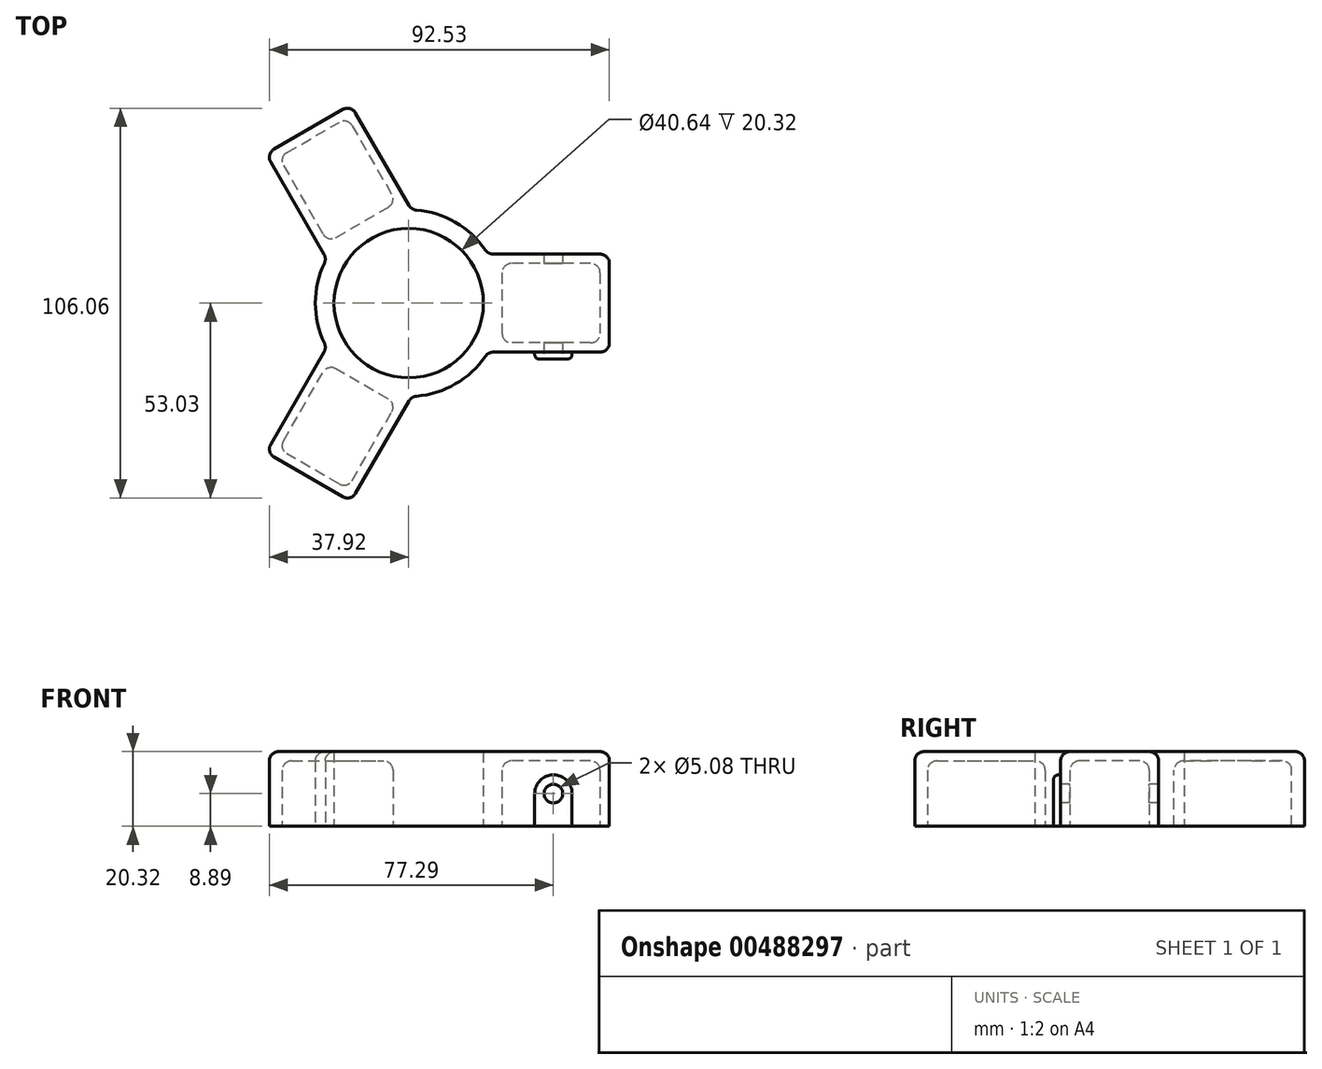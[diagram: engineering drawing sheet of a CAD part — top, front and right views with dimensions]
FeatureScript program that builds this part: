
annotation { "Feature Type Name" : "Feature", "Feature Type Description" : "" }
export const myFeature = defineFeature(function(context is Context, id is Id, definition is map)
    precondition{}
    {
        {
            var Q0;
            Q0=qCreatedBy(makeId("Top.planeOp"),FACE);
            var sketch = newSketch(context, id + "F0", { "sketchPlane" : qUnion([Q0])});
            skCircle(sketch, "E0", {"center": v(0, 0) * mm, "radius": 20.32 * mm});
            skCircle(sketch, "E1.0", {"center": v(0, 0) * mm, "radius": 25.4 * mm});
            skSolve(sketch);
        }
        {
            var Q0;
            Q0=makeQuery(id+"F0.imprint","IMPRINT",FACE,{"disambiguationData":[TD([[makeQuery(id+"F0.imprint","IMPRINT",EDGE,{"derivedFrom":sQuery(id+"F0.wireOp",EDGE,"E0")}),-1.0]])]});
            extrude(context, id + "F1", {"entities" : qUnion([Q0]), "depth" : 20.32 * mm});
        }
        {
            var Q0;
            Q0=qCreatedBy(makeId("Top.planeOp"),FACE);
            var sketch = newSketch(context, id + "F2", { "sketchPlane" : qUnion([Q0])});
            skLineSegment(sketch, "E2.bottom", {"start": v(54.61, 13.34) * mm, "end": v(20.32, 13.34) * mm});
            skLineSegment(sketch, "E2.top", {"start": v(54.61, -13.33) * mm, "end": v(20.32, -13.33) * mm});
            skLineSegment(sketch, "E2.left", {"start": v(54.61, 13.34) * mm, "end": v(54.61, -13.33) * mm});
            skLineSegment(sketch, "E2.right", {"start": v(20.32, 13.34) * mm, "end": v(20.32, -13.33) * mm});
            skPoint(sketch, "E2.middle", {"position": v(37.47, 0) * mm});
            skLineSegment(sketch, "E3.1.0", {"start": v(-21.7, 10.93) * mm, "end": v(1.39, 24.27) * mm});
            skLineSegment(sketch, "E3.1.1", {"start": v(-38.85, 40.63) * mm, "end": v(-15.76, 53.96) * mm});
            skLineSegment(sketch, "E3.1.2", {"start": v(-15.76, 53.96) * mm, "end": v(1.39, 24.27) * mm});
            skLineSegment(sketch, "E3.1.3", {"start": v(-38.85, 40.63) * mm, "end": v(-21.7, 10.93) * mm});
            skPoint(sketch, "E3.1.4", {"position": v(-18.73, 32.45) * mm});
            skLineSegment(sketch, "E3.2.0", {"start": v(1.39, -24.27) * mm, "end": v(-21.7, -10.93) * mm});
            skLineSegment(sketch, "E3.2.1", {"start": v(-15.76, -53.96) * mm, "end": v(-38.85, -40.63) * mm});
            skLineSegment(sketch, "E3.2.2", {"start": v(-38.85, -40.63) * mm, "end": v(-21.7, -10.93) * mm});
            skLineSegment(sketch, "E3.2.3", {"start": v(-15.76, -53.96) * mm, "end": v(1.39, -24.27) * mm});
            skPoint(sketch, "E3.2.4", {"position": v(-18.73, -32.45) * mm});
            skPoint(sketch, "E3.center", {"position": v(0, 0) * mm});
            skLineSegment(sketch, "E4.0", {"start": v(52.07, 10.8) * mm, "end": v(25.4, 10.8) * mm});
            skLineSegment(sketch, "E4.1", {"start": v(52.07, 10.8) * mm, "end": v(52.07, -10.8) * mm});
            skLineSegment(sketch, "E4.2", {"start": v(52.07, -10.8) * mm, "end": v(25.4, -10.8) * mm});
            skLineSegment(sketch, "E4.3", {"start": v(25.4, 10.8) * mm, "end": v(25.4, -10.8) * mm});
            skLineSegment(sketch, "E5.1.0", {"start": v(-35.38, 39.7) * mm, "end": v(-22.05, 16.6) * mm});
            skLineSegment(sketch, "E5.1.2", {"start": v(-35.38, 39.7) * mm, "end": v(-16.69, 50.5) * mm});
            skLineSegment(sketch, "E5.1.3", {"start": v(-16.69, 50.5) * mm, "end": v(-3.35, 27.4) * mm});
            skLineSegment(sketch, "E5.1.4", {"start": v(-22.05, 16.6) * mm, "end": v(-3.35, 27.4) * mm});
            skLineSegment(sketch, "E5.2.0", {"start": v(-16.69, -50.5) * mm, "end": v(-3.35, -27.4) * mm});
            skLineSegment(sketch, "E5.2.2", {"start": v(-16.69, -50.5) * mm, "end": v(-35.38, -39.7) * mm});
            skLineSegment(sketch, "E5.2.3", {"start": v(-35.38, -39.7) * mm, "end": v(-22.05, -16.6) * mm});
            skLineSegment(sketch, "E5.2.4", {"start": v(-3.35, -27.4) * mm, "end": v(-22.05, -16.6) * mm});
            skSolve(sketch);
        }
        {
            var Q0;
            Q0=makeQuery(id+"F2.imprint","IMPRINT",FACE,{"disambiguationData":[TD([[makeQuery(id+"F2.imprint","IMPRINT",EDGE,{"derivedFrom":sQuery(id+"F2.wireOp",EDGE,"E3.1.0")}),1.0]])]});
            var Q1;
            Q1=makeQuery(id+"F2.imprint","IMPRINT",FACE,{"disambiguationData":[TD([[makeQuery(id+"F2.imprint","IMPRINT",EDGE,{"derivedFrom":sQuery(id+"F2.wireOp",EDGE,"E3.2.0")}),1.0]])]});
            var Q2;
            Q2=makeQuery(id+"F2.imprint","IMPRINT",FACE,{"disambiguationData":[TD([[makeQuery(id+"F2.imprint","IMPRINT",EDGE,{"derivedFrom":sQuery(id+"F2.wireOp",EDGE,"E2.bottom")}),1.0]])]});
            extrude(context, id + "F3", {"entities" : qUnion([Q0, Q1, Q2]), "operationType" : NewBodyOperationType.ADD, "depth" : 20.32 * mm});
        }
        {
            var Q0;
            Q0=makeQuery(id+"F3.boolean.opBoolean","MERGE",FACE,{"derivedFrom":[makeQuery(id+"F1.opExtrude","CAP_FACE",FACE,{"disambiguationData":[OSD([sQuery(id+"F0.wireOp",EDGE,"E0"),sQuery(id+"F0.wireOp",EDGE,"E1.0")])],"isStart":false}),makeQuery(id+"F3.opExtrude","CAP_FACE",FACE,{"disambiguationData":[OSD([sQuery(id+"F2.wireOp",EDGE,"E2.bottom"),sQuery(id+"F2.wireOp",EDGE,"E2.top"),sQuery(id+"F2.wireOp",EDGE,"E2.left"),sQuery(id+"F2.wireOp",EDGE,"E2.right"),sQuery(id+"F2.wireOp",EDGE,"E4.0"),sQuery(id+"F2.wireOp",EDGE,"E4.1"),sQuery(id+"F2.wireOp",EDGE,"E4.2"),sQuery(id+"F2.wireOp",EDGE,"E4.3")])],"isStart":false}),makeQuery(id+"F3.opExtrude","CAP_FACE",FACE,{"disambiguationData":[OSD([sQuery(id+"F2.wireOp",EDGE,"E3.1.0"),sQuery(id+"F2.wireOp",EDGE,"E3.1.1"),sQuery(id+"F2.wireOp",EDGE,"E3.1.2"),sQuery(id+"F2.wireOp",EDGE,"E3.1.3"),sQuery(id+"F2.wireOp",EDGE,"E5.1.0"),sQuery(id+"F2.wireOp",EDGE,"E5.1.2"),sQuery(id+"F2.wireOp",EDGE,"E5.1.3"),sQuery(id+"F2.wireOp",EDGE,"E5.1.4")])],"isStart":false}),makeQuery(id+"F3.opExtrude","CAP_FACE",FACE,{"disambiguationData":[OSD([sQuery(id+"F2.wireOp",EDGE,"E3.2.0"),sQuery(id+"F2.wireOp",EDGE,"E3.2.1"),sQuery(id+"F2.wireOp",EDGE,"E3.2.2"),sQuery(id+"F2.wireOp",EDGE,"E3.2.3"),sQuery(id+"F2.wireOp",EDGE,"E5.2.0"),sQuery(id+"F2.wireOp",EDGE,"E5.2.2"),sQuery(id+"F2.wireOp",EDGE,"E5.2.3"),sQuery(id+"F2.wireOp",EDGE,"E5.2.4")])],"isStart":false})]});
            var sketch = newSketch(context, id + "F4", { "sketchPlane" : qUnion([Q0])});
            skLineSegment(sketch, "E6.0", {"start": v(52.07, 10.8) * mm, "end": v(52.07, -10.8) * mm});
            skLineSegment(sketch, "E6.1", {"start": v(52.07, -10.8) * mm, "end": v(25.4, -10.8) * mm});
            skArc(sketch, "E6.2", {"start": v(21.59, -10.78) * mm, "mid": v(24.13, 0) * mm, "end": v(21.6, 10.78) * mm});
            skLineSegment(sketch, "E6.3", {"start": v(52.07, 10.8) * mm, "end": v(25.4, 10.8) * mm});
            skLineSegment(sketch, "E7.1.0", {"start": v(-35.38, 39.7) * mm, "end": v(-16.69, 50.5) * mm});
            skLineSegment(sketch, "E7.1.1", {"start": v(-16.69, 50.5) * mm, "end": v(-3.35, 27.4) * mm});
            skArc(sketch, "E7.1.2", {"start": v(-1.46, 24.09) * mm, "mid": v(-12.06, 20.9) * mm, "end": v(-20.13, 13.3) * mm});
            skLineSegment(sketch, "E7.1.3", {"start": v(-35.38, 39.7) * mm, "end": v(-22.05, 16.6) * mm});
            skLineSegment(sketch, "E7.2.0", {"start": v(-16.69, -50.5) * mm, "end": v(-35.38, -39.7) * mm});
            skLineSegment(sketch, "E7.2.1", {"start": v(-35.38, -39.7) * mm, "end": v(-22.05, -16.6) * mm});
            skArc(sketch, "E7.2.2", {"start": v(-20.13, -13.3) * mm, "mid": v(-12.07, -20.9) * mm, "end": v(-1.46, -24.09) * mm});
            skLineSegment(sketch, "E7.2.3", {"start": v(-16.69, -50.5) * mm, "end": v(-3.35, -27.4) * mm});
            skSolve(sketch);
        }
        {
            var Q0;
            Q0=makeQuery(id+"F4.imprint","IMPRINT",FACE,{"disambiguationData":[TD([[makeQuery(id+"F4.imprint","IMPRINT",EDGE,{"derivedFrom":sQuery(id+"F4.wireOp",EDGE,"E7.1.0")}),-1.0]])]});
            var Q1;
            Q1=makeQuery(id+"F4.imprint","IMPRINT",FACE,{"disambiguationData":[TD([[makeQuery(id+"F4.imprint","IMPRINT",EDGE,{"derivedFrom":sQuery(id+"F4.wireOp",EDGE,"E6.0")}),-1.0]])]});
            var Q2;
            Q2=makeQuery(id+"F4.imprint","IMPRINT",FACE,{"disambiguationData":[TD([[makeQuery(id+"F4.imprint","IMPRINT",EDGE,{"derivedFrom":sQuery(id+"F4.wireOp",EDGE,"E7.2.0")}),-1.0]])]});
            extrude(context, id + "F5", {"entities" : qUnion([Q0, Q1, Q2]), "operationType" : NewBodyOperationType.ADD, "oppositeDirection" : true, "depth" : 2.54 * mm});
        }
        {
            var Q0;
            Q0=makeQuery(id+"F3.opExtrude","SWEPT_FACE",FACE,{"disambiguationData":[OSD([sQuery(id+"F2.wireOp",EDGE,"E2.top")])]});
            var sketch = newSketch(context, id + "F6", { "sketchPlane" : qUnion([Q0])});
            skCircle(sketch, "E8", {"center": v(39.37, 8.9) * mm, "radius": 2.54 * mm});
            skSolve(sketch);
        }
        {
            var Q0;
            Q0=makeQuery(id+"F6.imprint","IMPRINT",FACE,{"disambiguationData":[TD([[makeQuery(id+"F6.imprint","IMPRINT",EDGE,{"derivedFrom":sQuery(id+"F6.wireOp",EDGE,"E8")}),1.0]])]});
            extrude(context, id + "F7", {"entities" : qUnion([Q0]), "operationType" : NewBodyOperationType.REMOVE, "endBound" : BoundingType.THROUGH_ALL, "oppositeDirection" : true, "depth" : 25.4 * mm});
        }
        {
            var Q0;
            Q0=makeQuery(id+"F3.opExtrude","SWEPT_FACE",FACE,{"disambiguationData":[OSD([sQuery(id+"F2.wireOp",EDGE,"E2.top")])]});
            var sketch = newSketch(context, id + "F8", { "sketchPlane" : qUnion([Q0])});
            skArc(sketch, "E9", {"start": v(44.45, 8.9) * mm, "mid": v(39.37, 13.97) * mm, "end": v(34.3, 8.9) * mm});
            skLineSegment(sketch, "E10.top", {"start": v(34.3, 0) * mm, "end": v(44.45, 0) * mm});
            skLineSegment(sketch, "E10.left", {"start": v(34.3, 8.9) * mm, "end": v(34.3, 0) * mm});
            skLineSegment(sketch, "E10.right", {"start": v(44.45, 8.9) * mm, "end": v(44.45, 0) * mm});
            skCircle(sketch, "E11.0", {"center": v(39.37, 8.9) * mm, "radius": 2.54 * mm});
            skSolve(sketch);
        }
        {
            var Q0;
            Q0=makeQuery(id+"F8.imprint","IMPRINT",FACE,{"disambiguationData":[TD([[makeQuery(id+"F8.imprint","IMPRINT",EDGE,{"derivedFrom":sQuery(id+"F8.wireOp",EDGE,"E9")}),1.0]])]});
            extrude(context, id + "F9", {"entities" : qUnion([Q0]), "operationType" : NewBodyOperationType.ADD, "depth" : 1.9 * mm});
        }
        {
            var Q0;
            Q0=makeQuery(id+"F9.opExtrude","CAP_EDGE",EDGE,{"disambiguationData":[OSD([sQuery(id+"F8.wireOp",EDGE,"E10.right")])],"isStart":false});
            fillet(context, id + "F10", {"entities" : qUnion([Q0]), "radius" : 1.27 * mm, "tangentPropagation" : true, "allowEdgeOverflow" : false});
        }
        {
            var Q0;
            Q0=makeQuery(id+"F5.opExtrude","CAP_FACE",FACE,{"disambiguationData":[OSD([sQuery(id+"F2.wireOp",EDGE,"E4.3"),sQuery(id+"F4.wireOp",EDGE,"E6.0"),sQuery(id+"F4.wireOp",EDGE,"E6.1"),sQuery(id+"F4.wireOp",EDGE,"E6.3")])],"isStart":false});
            var Q1;
            Q1=makeQuery(id+"F3.opExtrude","SWEPT_EDGE",EDGE,{"disambiguationData":[OSD([sQuery(id+"F2.wireOp",EDGE,"E4.2"),sQuery(id+"F2.wireOp",EDGE,"E4.3")])]});
            var Q2;
            Q2=makeQuery(id+"F3.opExtrude","SWEPT_EDGE",EDGE,{"disambiguationData":[OSD([sQuery(id+"F2.wireOp",EDGE,"E4.1"),sQuery(id+"F2.wireOp",EDGE,"E4.2")])]});
            var Q3;
            Q3=makeQuery(id+"F3.opExtrude","SWEPT_EDGE",EDGE,{"disambiguationData":[OSD([sQuery(id+"F2.wireOp",EDGE,"E4.0"),sQuery(id+"F2.wireOp",EDGE,"E4.1")])]});
            var Q4;
            Q4=makeQuery(id+"F3.opExtrude","SWEPT_EDGE",EDGE,{"disambiguationData":[OSD([sQuery(id+"F2.wireOp",EDGE,"E4.0"),sQuery(id+"F2.wireOp",EDGE,"E4.3")])]});
            var Q5;
            Q5=makeQuery(id+"F5.opExtrude","CAP_FACE",FACE,{"disambiguationData":[OSD([sQuery(id+"F2.wireOp",EDGE,"E5.2.4"),sQuery(id+"F4.wireOp",EDGE,"E7.2.0"),sQuery(id+"F4.wireOp",EDGE,"E7.2.1"),sQuery(id+"F4.wireOp",EDGE,"E7.2.3")])],"isStart":false});
            var Q6;
            Q6=makeQuery(id+"F3.opExtrude","SWEPT_EDGE",EDGE,{"disambiguationData":[OSD([sQuery(id+"F2.wireOp",EDGE,"E5.2.0"),sQuery(id+"F2.wireOp",EDGE,"E5.2.2")])]});
            var Q7;
            Q7=makeQuery(id+"F3.opExtrude","SWEPT_EDGE",EDGE,{"disambiguationData":[OSD([sQuery(id+"F2.wireOp",EDGE,"E5.2.0"),sQuery(id+"F2.wireOp",EDGE,"E5.2.4")])]});
            var Q8;
            Q8=makeQuery(id+"F3.opExtrude","SWEPT_EDGE",EDGE,{"disambiguationData":[OSD([sQuery(id+"F2.wireOp",EDGE,"E5.2.3"),sQuery(id+"F2.wireOp",EDGE,"E5.2.4")])]});
            var Q9;
            Q9=makeQuery(id+"F3.opExtrude","SWEPT_EDGE",EDGE,{"disambiguationData":[OSD([sQuery(id+"F2.wireOp",EDGE,"E5.2.2"),sQuery(id+"F2.wireOp",EDGE,"E5.2.3")])]});
            var Q10;
            Q10=makeQuery(id+"F5.opExtrude","CAP_FACE",FACE,{"disambiguationData":[OSD([sQuery(id+"F2.wireOp",EDGE,"E5.1.4"),sQuery(id+"F4.wireOp",EDGE,"E7.1.0"),sQuery(id+"F4.wireOp",EDGE,"E7.1.1"),sQuery(id+"F4.wireOp",EDGE,"E7.1.3")])],"isStart":false});
            var Q11;
            Q11=makeQuery(id+"F3.opExtrude","SWEPT_EDGE",EDGE,{"disambiguationData":[OSD([sQuery(id+"F2.wireOp",EDGE,"E5.1.0"),sQuery(id+"F2.wireOp",EDGE,"E5.1.2")])]});
            var Q12;
            Q12=makeQuery(id+"F3.opExtrude","SWEPT_EDGE",EDGE,{"disambiguationData":[OSD([sQuery(id+"F2.wireOp",EDGE,"E5.1.3"),sQuery(id+"F2.wireOp",EDGE,"E5.1.4")])]});
            var Q13;
            Q13=makeQuery(id+"F3.opExtrude","SWEPT_EDGE",EDGE,{"disambiguationData":[OSD([sQuery(id+"F2.wireOp",EDGE,"E5.1.2"),sQuery(id+"F2.wireOp",EDGE,"E5.1.3")])]});
            var Q14;
            Q14=makeQuery(id+"F3.opExtrude","SWEPT_EDGE",EDGE,{"disambiguationData":[OSD([sQuery(id+"F2.wireOp",EDGE,"E5.1.0"),sQuery(id+"F2.wireOp",EDGE,"E5.1.4")])]});
            fillet(context, id + "F11", {"entities" : qUnion([Q0, Q1, Q2, Q3, Q4, Q5, Q6, Q7, Q8, Q9, Q10, Q11, Q12, Q13, Q14]), "radius" : 2.54 * mm, "tangentPropagation" : true, "allowEdgeOverflow" : false});
        }
        {
            var Q0;
            Q0=makeQuery(id+"F3.boolean.opBoolean","INTERSECT",EDGE,{"derivedFrom":[makeQuery(id+"F1.opExtrude","SWEPT_FACE",FACE,{"disambiguationData":[OSD([sQuery(id+"F0.wireOp",EDGE,"E1.0")])]}),makeQuery(id+"F3.opExtrude","SWEPT_FACE",FACE,{"disambiguationData":[OSD([sQuery(id+"F2.wireOp",EDGE,"E3.2.3")])]})]});
            var Q1;
            Q1=makeQuery(id+"F3.boolean.opBoolean","INTERSECT",EDGE,{"derivedFrom":[makeQuery(id+"F1.opExtrude","SWEPT_FACE",FACE,{"disambiguationData":[OSD([sQuery(id+"F0.wireOp",EDGE,"E1.0")])]}),makeQuery(id+"F3.opExtrude","SWEPT_FACE",FACE,{"disambiguationData":[OSD([sQuery(id+"F2.wireOp",EDGE,"E2.top")])]})]});
            var Q2;
            Q2=makeQuery(id+"F3.boolean.opBoolean","INTERSECT",EDGE,{"derivedFrom":[makeQuery(id+"F1.opExtrude","SWEPT_FACE",FACE,{"disambiguationData":[OSD([sQuery(id+"F0.wireOp",EDGE,"E1.0")])]}),makeQuery(id+"F3.opExtrude","SWEPT_FACE",FACE,{"disambiguationData":[OSD([sQuery(id+"F2.wireOp",EDGE,"E2.bottom")])]})]});
            var Q3;
            Q3=makeQuery(id+"F3.boolean.opBoolean","INTERSECT",EDGE,{"derivedFrom":[makeQuery(id+"F1.opExtrude","SWEPT_FACE",FACE,{"disambiguationData":[OSD([sQuery(id+"F0.wireOp",EDGE,"E1.0")])]}),makeQuery(id+"F3.opExtrude","SWEPT_FACE",FACE,{"disambiguationData":[OSD([sQuery(id+"F2.wireOp",EDGE,"E3.1.2")])]})]});
            var Q4;
            Q4=makeQuery(id+"F3.boolean.opBoolean","INTERSECT",EDGE,{"derivedFrom":[makeQuery(id+"F1.opExtrude","SWEPT_FACE",FACE,{"disambiguationData":[OSD([sQuery(id+"F0.wireOp",EDGE,"E1.0")])]}),makeQuery(id+"F3.opExtrude","SWEPT_FACE",FACE,{"disambiguationData":[OSD([sQuery(id+"F2.wireOp",EDGE,"E3.2.2")])]})]});
            var Q5;
            Q5=makeQuery(id+"F3.boolean.opBoolean","INTERSECT",EDGE,{"derivedFrom":[makeQuery(id+"F1.opExtrude","SWEPT_FACE",FACE,{"disambiguationData":[OSD([sQuery(id+"F0.wireOp",EDGE,"E1.0")])]}),makeQuery(id+"F3.opExtrude","SWEPT_FACE",FACE,{"disambiguationData":[OSD([sQuery(id+"F2.wireOp",EDGE,"E3.1.3")])]})]});
            var Q6;
            Q6=makeQuery(id+"F3.opExtrude","SWEPT_EDGE",EDGE,{"disambiguationData":[OSD([sQuery(id+"F2.wireOp",EDGE,"E3.2.1"),sQuery(id+"F2.wireOp",EDGE,"E3.2.3")])]});
            var Q7;
            Q7=makeQuery(id+"F3.opExtrude","SWEPT_EDGE",EDGE,{"disambiguationData":[OSD([sQuery(id+"F2.wireOp",EDGE,"E2.top"),sQuery(id+"F2.wireOp",EDGE,"E2.left")])]});
            var Q8;
            Q8=makeQuery(id+"F3.opExtrude","SWEPT_EDGE",EDGE,{"disambiguationData":[OSD([sQuery(id+"F2.wireOp",EDGE,"E2.bottom"),sQuery(id+"F2.wireOp",EDGE,"E2.left")])]});
            var Q9;
            Q9=makeQuery(id+"F3.opExtrude","SWEPT_EDGE",EDGE,{"disambiguationData":[OSD([sQuery(id+"F2.wireOp",EDGE,"E3.1.1"),sQuery(id+"F2.wireOp",EDGE,"E3.1.2")])]});
            var Q10;
            Q10=makeQuery(id+"F3.opExtrude","SWEPT_EDGE",EDGE,{"disambiguationData":[OSD([sQuery(id+"F2.wireOp",EDGE,"E3.1.1"),sQuery(id+"F2.wireOp",EDGE,"E3.1.3")])]});
            var Q11;
            Q11=makeQuery(id+"F3.opExtrude","SWEPT_EDGE",EDGE,{"disambiguationData":[OSD([sQuery(id+"F2.wireOp",EDGE,"E3.2.1"),sQuery(id+"F2.wireOp",EDGE,"E3.2.2")])]});
            fillet(context, id + "F12", {"entities" : qUnion([Q0, Q1, Q2, Q3, Q4, Q5, Q6, Q7, Q8, Q9, Q10, Q11]), "radius" : 2.54 * mm, "tangentPropagation" : true, "allowEdgeOverflow" : false});
        }
        {
            var Q0;
            Q0=makeQuery(id+"F3.opExtrude","CAP_EDGE",EDGE,{"disambiguationData":[OSD([sQuery(id+"F2.wireOp",EDGE,"E2.bottom")])],"isStart":false});
            fillet(context, id + "F13", {"entities" : qUnion([Q0]), "radius" : 2.54 * mm, "tangentPropagation" : true, "allowEdgeOverflow" : false});
        }
    });
